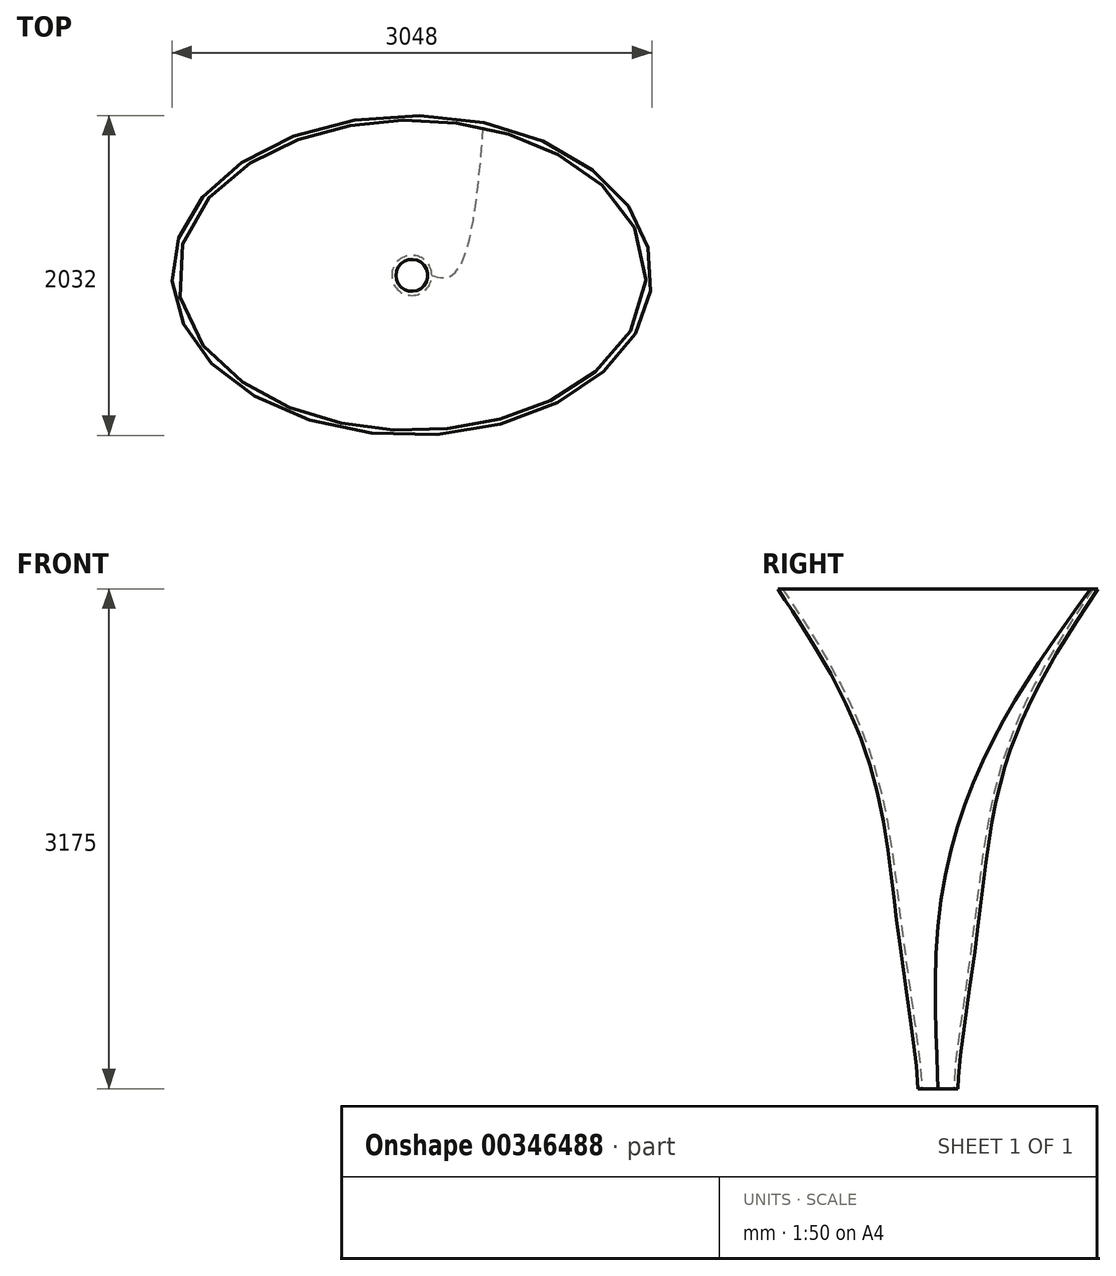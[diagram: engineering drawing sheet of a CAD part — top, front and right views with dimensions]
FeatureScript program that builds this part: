
annotation { "Feature Type Name" : "Feature", "Feature Type Description" : "" }
export const myFeature = defineFeature(function(context is Context, id is Id, definition is map)
    precondition{}
    {
        {
            var Q0;
            Q0=qCreatedBy(makeId("Top.planeOp"),FACE);
            var sketch = newSketch(context, id + "F0", { "sketchPlane" : qUnion([Q0])});
            skCircle(sketch, "E0", {"center": v(-3, 3.81) * mm, "radius": 127 * mm});
            skSolve(sketch);
        }
        {
            var Q0;
            Q0=makeQuery(id+"F0.imprint","IMPRINT",FACE,{"disambiguationData":[TD([[makeQuery(id+"F0.imprint","IMPRINT",EDGE,{"derivedFrom":sQuery(id+"F0.wireOp",EDGE,"E0")}),1.0]])]});
            cPlane(context, id + "F1", {"entities" : qUnion([Q0]), "cplaneType" : CPlaneType.OFFSET, "offset" : 1016 * mm, "width" : 152.4 * mm, "height" : 152.4 * mm});
        }
        {
            var Q0;
            Q0=qCreatedBy(id+"F1.planeOp",FACE);
            var sketch = newSketch(context, id + "F2", { "sketchPlane" : qUnion([Q0])});
            skCircle(sketch, "E1", {"center": v(-3, 3.81) * mm, "radius": 254 * mm});
            skSolve(sketch);
        }
        {
            var Q0;
            Q0=makeQuery(id+"F2.imprint","IMPRINT",FACE,{"disambiguationData":[TD([[makeQuery(id+"F2.imprint","IMPRINT",EDGE,{"derivedFrom":sQuery(id+"F2.wireOp",EDGE,"E1")}),1.0]])]});
            cPlane(context, id + "F3", {"entities" : qUnion([Q0]), "cplaneType" : CPlaneType.OFFSET, "offset" : 2159 * mm, "width" : 152.4 * mm, "height" : 152.4 * mm});
        }
        {
            var Q0;
            Q0=qCreatedBy(id+"F3.planeOp",FACE);
            var sketch = newSketch(context, id + "F4", { "sketchPlane" : qUnion([Q0])});
            skEllipse(sketch, "E2", {"center": v(-3, 3.81) * mm, "majorRadius": 1524 * mm, "minorRadius": 1016 * mm, "majorAxis": v(1, 0)});
            skSolve(sketch);
        }
        {
            var Q0;
            Q0=makeQuery(id+"F0.imprint","IMPRINT",FACE,{"disambiguationData":[TD([[makeQuery(id+"F0.imprint","IMPRINT",EDGE,{"derivedFrom":sQuery(id+"F0.wireOp",EDGE,"E0")}),1.0]])]});
            var Q1;
            Q1=makeQuery(id+"F2.imprint","IMPRINT",FACE,{"disambiguationData":[TD([[makeQuery(id+"F2.imprint","IMPRINT",EDGE,{"derivedFrom":sQuery(id+"F2.wireOp",EDGE,"E1")}),1.0]])]});
            var Q2;
            Q2=makeQuery(id+"F4.imprint","IMPRINT",FACE,{"disambiguationData":[TD([[makeQuery(id+"F4.imprint","IMPRINT",EDGE,{"derivedFrom":sQuery(id+"F4.wireOp",EDGE,"E2")}),1.0]])]});
            loft(context, id + "F5", {"startCondition" : LoftEndDerivativeType.NORMAL_TO_PROFILE, "startMagnitude" : 0.5, "endCondition" : LoftEndDerivativeType.NORMAL_TO_PROFILE, "endMagnitude" : 0, "sheetProfilesArray" : [{ "sheetProfileEntities" : qUnion([Q0]) }, { "sheetProfileEntities" : qUnion([Q1]) }, { "sheetProfileEntities" : qUnion([Q2]) }]});
        }
        {
            var Q0;
            Q0=makeQuery(id+"F5.opLoft","CAP_FACE",FACE,{"disambiguationData":[OSD([makeQuery(id+"F4.imprint","IMPRINT",FACE,{"disambiguationData":[TD([[makeQuery(id+"F4.imprint","IMPRINT",EDGE,{"derivedFrom":sQuery(id+"F4.wireOp",EDGE,"E2")}),1.0]])]})])],"isStart":true});
            var Q1;
            Q1=makeQuery(id+"F5.opLoft","CAP_FACE",FACE,{"disambiguationData":[OSD([makeQuery(id+"F0.imprint","IMPRINT",FACE,{"disambiguationData":[TD([[makeQuery(id+"F0.imprint","IMPRINT",EDGE,{"derivedFrom":sQuery(id+"F0.wireOp",EDGE,"E0")}),1.0]])]})])],"isStart":true});
            shell(context, id + "F6", {"entities" : qUnion([Q0, Q1]), "thickness" : 25.4 * mm});
        }
    });
